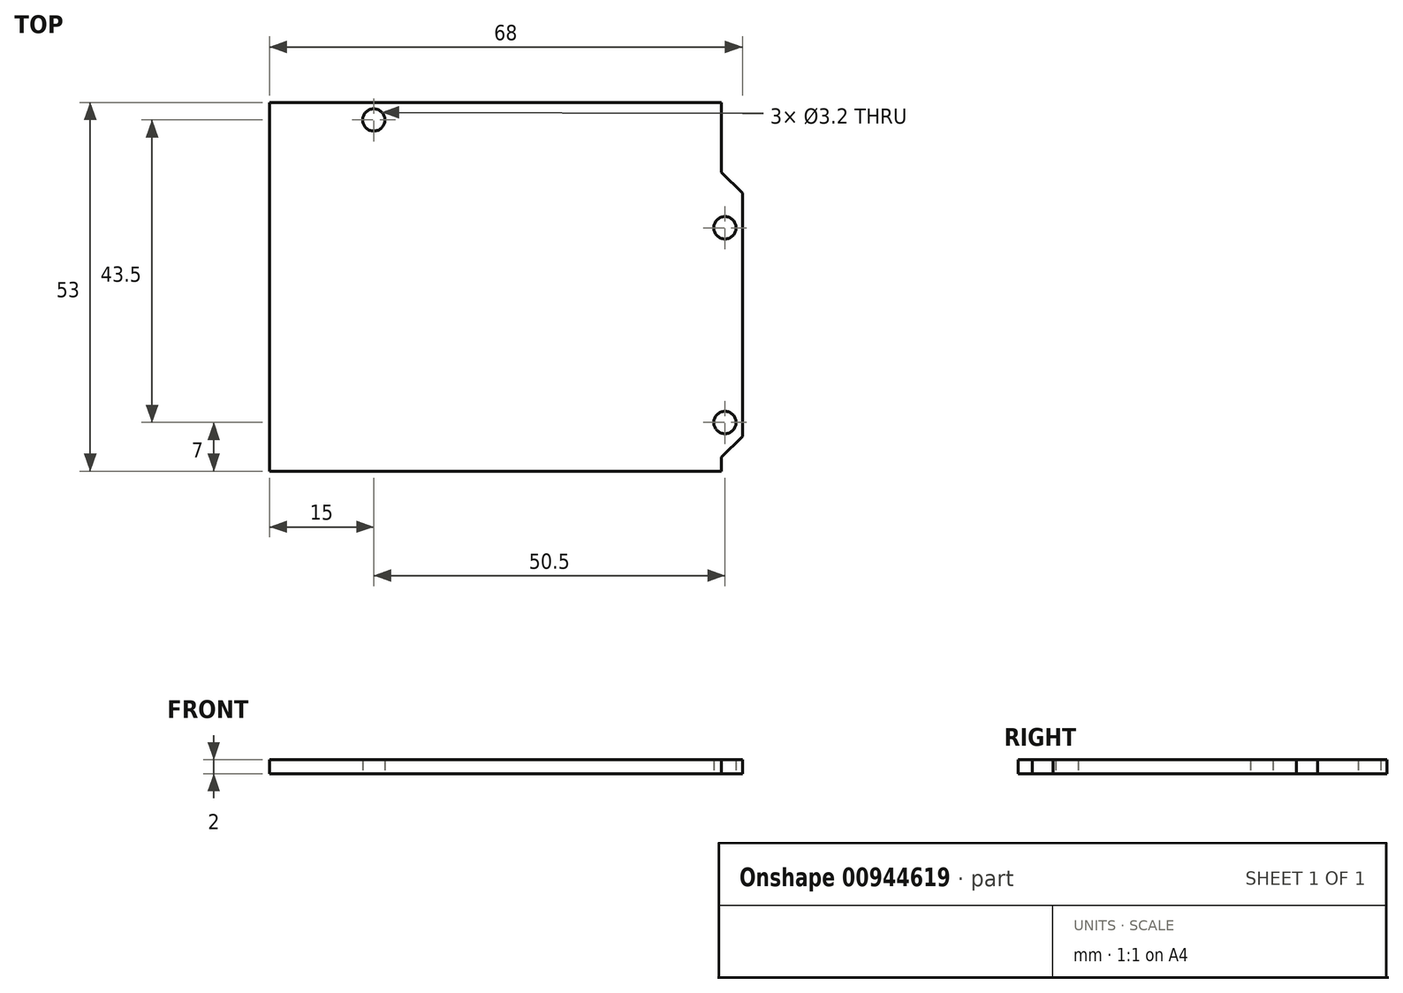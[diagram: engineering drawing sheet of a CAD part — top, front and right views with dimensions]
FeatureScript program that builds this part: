
annotation { "Feature Type Name" : "Feature", "Feature Type Description" : "" }
export const myFeature = defineFeature(function(context is Context, id is Id, definition is map)
    precondition{}
    {
        {
            var Q0;
            Q0=qCreatedBy(makeId("Top.planeOp"),FACE);
            var sketch = newSketch(context, id + "F0", { "sketchPlane" : qUnion([Q0])});
            skLineSegment(sketch, "E0.bottom", {"start": v(0, 26.5) * mm, "end": v(65, 26.5) * mm});
            skLineSegment(sketch, "E0.top", {"start": v(0, -26.5) * mm, "end": v(65, -26.5) * mm});
            skLineSegment(sketch, "E0.left", {"start": v(0, 26.5) * mm, "end": v(0, -26.5) * mm});
            skLineSegment(sketch, "E0.right", {"start": v(68, 13.5) * mm, "end": v(68, -21.5) * mm});
            skLineSegment(sketch, "E1", {"start": v(65, -26.5) * mm, "end": v(65, -24.5) * mm});
            skLineSegment(sketch, "E2", {"start": v(65, -24.5) * mm, "end": v(68, -21.5) * mm});
            skLineSegment(sketch, "E3", {"start": v(65, 26.5) * mm, "end": v(65, 16.5) * mm});
            skLineSegment(sketch, "E4", {"start": v(65, 16.5) * mm, "end": v(68, 13.5) * mm});
            skCircle(sketch, "E5", {"center": v(15, 24) * mm, "radius": 1.6 * mm});
            skCircle(sketch, "E6", {"center": v(65.5, 8.5) * mm, "radius": 1.6 * mm});
            skCircle(sketch, "E7", {"center": v(65.5, -19.5) * mm, "radius": 1.6 * mm});
            skSolve(sketch);
        }
        {
            var Q0;
            Q0 = qSketchRegion(id + "F0", true);
            extrude(context, id + "F1", {"entities" : qUnion([Q0]), "depth" : 2 * mm, "offsetDistance" : 25 * mm});
        }
    });
